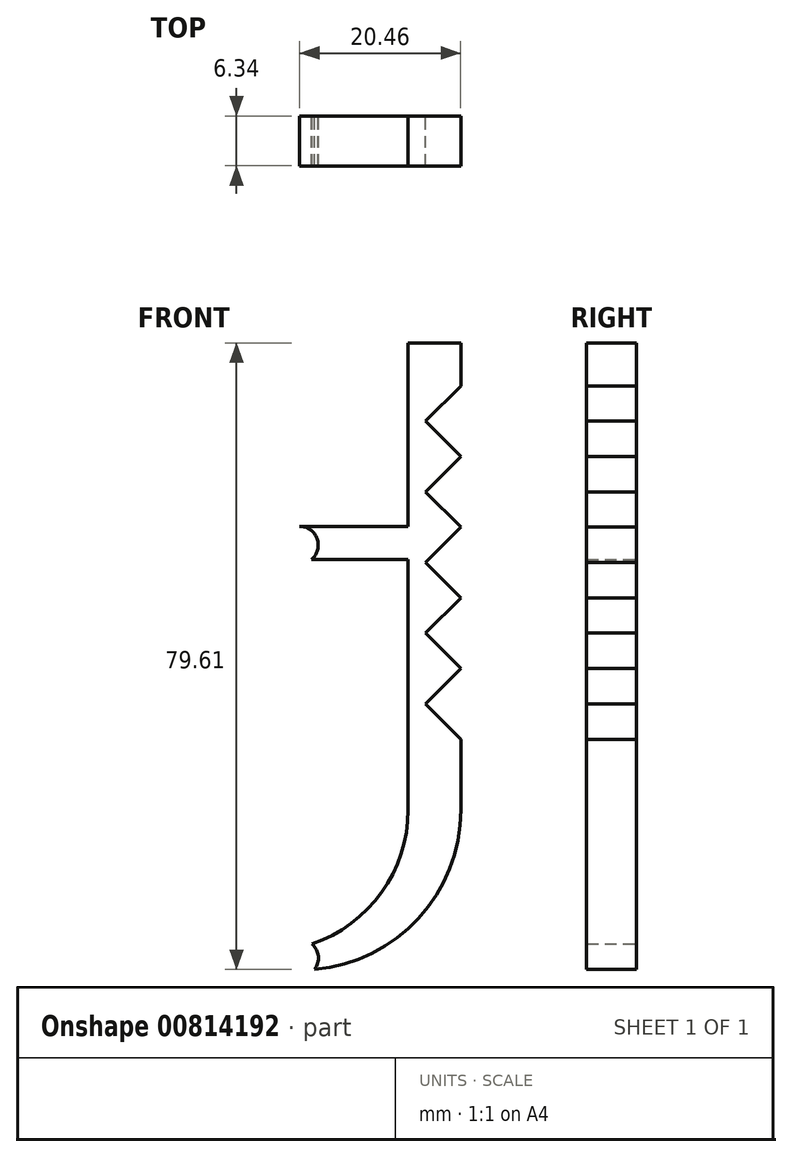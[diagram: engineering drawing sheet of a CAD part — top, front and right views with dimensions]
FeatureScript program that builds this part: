
annotation { "Feature Type Name" : "Feature", "Feature Type Description" : "" }
export const myFeature = defineFeature(function(context is Context, id is Id, definition is map)
    precondition{}
    {
        {
            var Q0;
            Q0=qCreatedBy(makeId("Front.planeOp"),FACE);
            var sketch = newSketch(context, id + "F0", { "sketchPlane" : qUnion([Q0])});
            skPoint(sketch, "E0.middle", {"position": v(0, -2.06) * mm});
            skCircle(sketch, "E1", {"center": v(0, -28.25) * mm, "radius": 2.38 * mm});
            skCircle(sketch, "E2", {"center": v(-0.02, 24.23) * mm, "radius": 2.38 * mm});
            skPoint(sketch, "E2.third.point", {"position": v(0, 26.61) * mm});
            skLineSegment(sketch, "E3", {"start": v(0, 26.61) * mm, "end": v(13.78, 26.61) * mm});
            skLineSegment(sketch, "E4", {"start": v(13.78, 26.61) * mm, "end": v(13.78, 22.4) * mm});
            skLineSegment(sketch, "E5", {"start": v(13.78, 22.4) * mm, "end": v(1.5, 22.4) * mm});
            skLineSegment(sketch, "E6", {"start": v(13.78, -9.43) * mm, "end": v(13.78, 26.61) * mm});
            skLineSegment(sketch, "E7", {"start": v(13.78, -9.43) * mm, "end": v(13.78, -9.43) * mm});
            skLineSegment(sketch, "E8", {"start": v(20.46, -9.43) * mm, "end": v(13.78, -9.43) * mm});
            skLineSegment(sketch, "E9", {"start": v(13.78, 26.61) * mm, "end": v(13.78, 49.9) * mm});
            skLineSegment(sketch, "E10", {"start": v(13.78, 49.9) * mm, "end": v(20.46, 49.9) * mm});
            skLineSegment(sketch, "E11", {"start": v(20.46, 49.9) * mm, "end": v(20.46, 44.45) * mm});
            skPoint(sketch, "E12.endSnap0", {"position": v(13.78, 8.6) * mm});
            skArc(sketch, "E13", {"start": v(1.89, -29.7) * mm, "mid": v(15.12, -23.17) * mm, "end": v(20.46, -9.43) * mm});
            skArc(sketch, "E14", {"start": v(1.57, -26.46) * mm, "mid": v(10.41, -19.9) * mm, "end": v(13.78, -9.43) * mm});
            skLineSegment(sketch, "E15", {"start": v(20.46, 44.45) * mm, "end": v(15.97, 39.96) * mm});
            skLineSegment(sketch, "E16", {"start": v(15.97, 39.96) * mm, "end": v(20.46, 35.47) * mm});
            skLineSegment(sketch, "E17", {"start": v(20.46, 35.47) * mm, "end": v(15.98, 30.98) * mm});
            skLineSegment(sketch, "E18", {"start": v(15.98, 30.98) * mm, "end": v(20.46, 26.5) * mm});
            skLineSegment(sketch, "E19", {"start": v(20.46, 26.5) * mm, "end": v(15.98, 22.01) * mm});
            skLineSegment(sketch, "E20", {"start": v(15.98, 22.01) * mm, "end": v(20.46, 17.53) * mm});
            skLineSegment(sketch, "E21", {"start": v(20.46, 17.53) * mm, "end": v(15.97, 13.04) * mm});
            skLineSegment(sketch, "E22", {"start": v(15.97, 13.04) * mm, "end": v(20.46, 8.55) * mm});
            skLineSegment(sketch, "E23", {"start": v(20.46, 8.55) * mm, "end": v(15.97, 4.06) * mm});
            skLineSegment(sketch, "E24", {"start": v(15.97, 4.06) * mm, "end": v(20.46, -0.43) * mm});
            skLineSegment(sketch, "E25", {"start": v(20.46, -0.43) * mm, "end": v(20.46, -9.43) * mm});
            skSolve(sketch);
        }
        {
            var Q0;
            {var subQ0=sQuery(id+"F0.wireOp",EDGE,"E10");Q0=makeQuery(id+"F0.imprint","IMPRINT",FACE,{"disambiguationData":[TD([[makeQuery(id+"F0.imprint","IMPRINT",EDGE,{"derivedFrom":subQ0}),-1.0]])]});}
            var Q1;
            {var subQ2=sQuery(id+"F0.wireOp",EDGE,"696b575a-0d74-4534-b700-7da15c48883a");Q1=makeQuery(id+"F0.imprint","IMPRINT",FACE,{"disambiguationData":[TD([[makeQuery(id+"F0.imprint","IMPRINT",EDGE,{"derivedFrom":subQ2}),-1.0]])]});}
            var Q2;
            {var subQ3=sQuery(id+"F0.wireOp",EDGE,"d24d036c-cbee-4841-a86e-5717c2eceecd");Q2=makeQuery(id+"F0.imprint","IMPRINT",FACE,{"disambiguationData":[TD([[makeQuery(id+"F0.imprint","IMPRINT",EDGE,{"derivedFrom":subQ3}),-1.0]])]});}
            var Q3;
            {var subQ0=sQuery(id+"F0.wireOp",EDGE,"467e9670-a318-44aa-bd07-a9da748eec49");Q3=makeQuery(id+"F0.imprint","IMPRINT",FACE,{"disambiguationData":[TD([[makeQuery(id+"F0.imprint","IMPRINT",EDGE,{"derivedFrom":subQ0}),-1.0]])]});}
            var Q4;
            {var subQ0=sQuery(id+"F0.wireOp",EDGE,"E8");Q4=makeQuery(id+"F0.imprint","IMPRINT",FACE,{"disambiguationData":[TD([[makeQuery(id+"F0.imprint","IMPRINT",EDGE,{"derivedFrom":subQ0}),-1.0]])]});}
            var Q5;
            Q5=makeQuery(id+"F0.imprint","IMPRINT",FACE,{"disambiguationData":[TD([[makeQuery(id+"F0.imprint","IMPRINT",EDGE,{"derivedFrom":sQuery(id+"F0.wireOp",EDGE,"E8")}),1.0]])]});
            var Q6;
            {var subQ2=sQuery(id+"F0.wireOp",EDGE,"E3");Q6=makeQuery(id+"F0.imprint","IMPRINT",FACE,{"disambiguationData":[TD([[makeQuery(id+"F0.imprint","IMPRINT",EDGE,{"derivedFrom":subQ2}),-1.0]])]});}
            extrude(context, id + "F1", {"entities" : qUnion([Q0, Q1, Q2, Q3, Q4, Q5, Q6]), "endBound" : BoundingType.SYMMETRIC, "depth" : 6.35 * mm, "offsetDistance" : 25.4 * mm});
        }
    });
